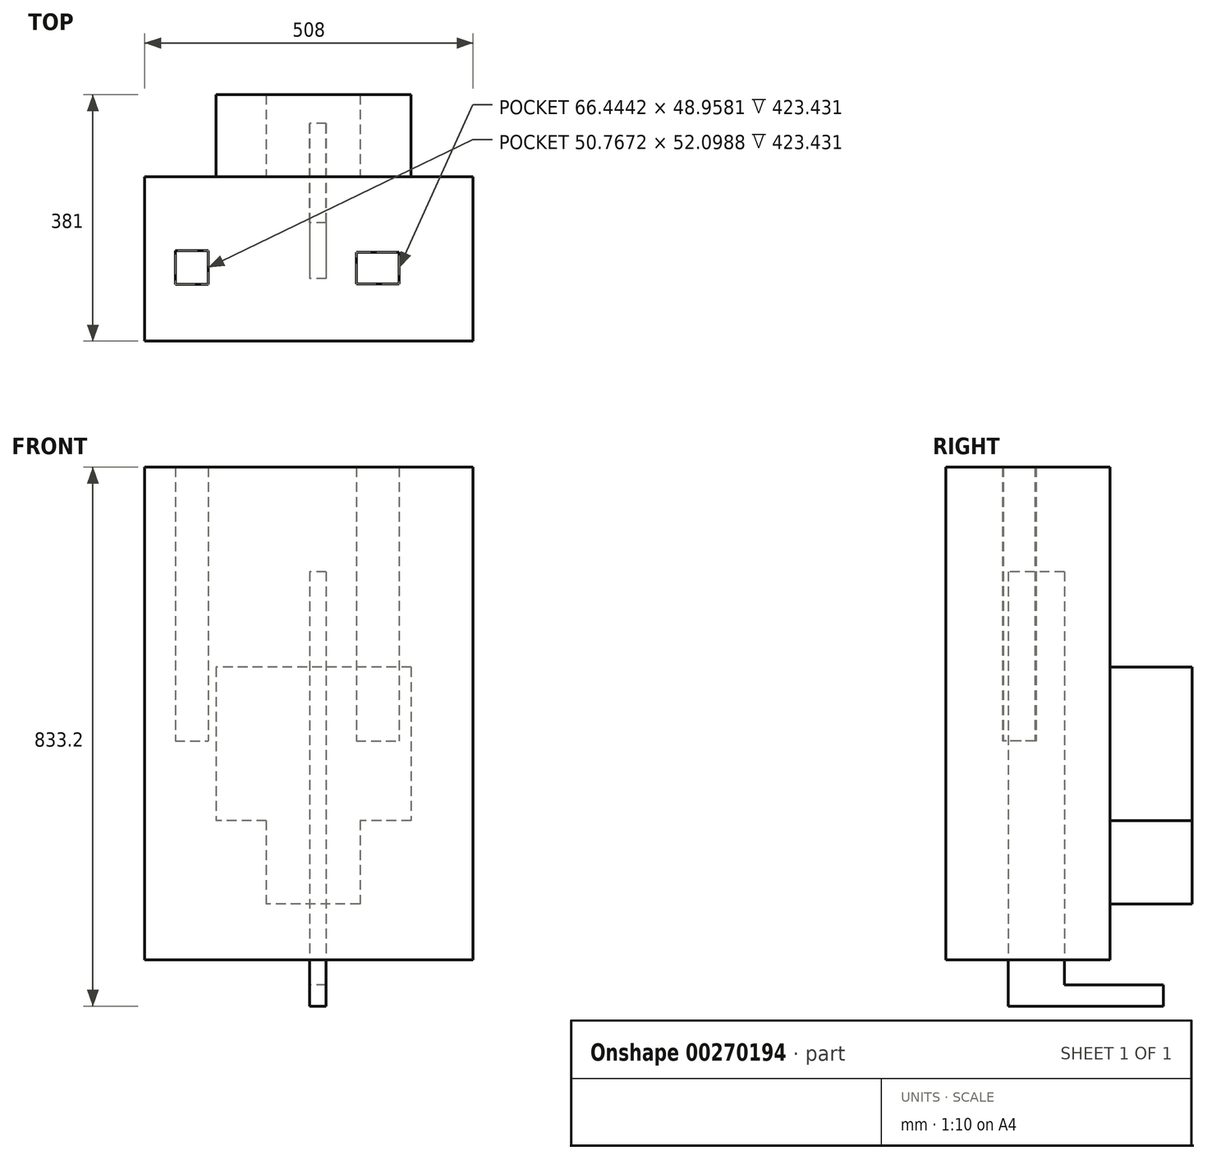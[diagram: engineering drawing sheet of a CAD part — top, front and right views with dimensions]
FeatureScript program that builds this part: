
annotation { "Feature Type Name" : "Feature", "Feature Type Description" : "" }
export const myFeature = defineFeature(function(context is Context, id is Id, definition is map)
    precondition{}
    {
        {
            var Q0;
            Q0=qCreatedBy(makeId("Front.planeOp"),FACE);
            var sketch = newSketch(context, id + "F0", { "sketchPlane" : qUnion([Q0])});
            skLineSegment(sketch, "E0.bottom", {"start": v(-255.3, 423.43) * mm, "end": v(252.7, 423.43) * mm});
            skLineSegment(sketch, "E0.top", {"start": v(-255.3, -338.57) * mm, "end": v(252.7, -338.57) * mm});
            skLineSegment(sketch, "E0.left", {"start": v(-255.3, 423.43) * mm, "end": v(-255.3, -338.57) * mm});
            skLineSegment(sketch, "E0.right", {"start": v(252.7, 423.43) * mm, "end": v(252.7, -338.57) * mm});
            skSolve(sketch);
        }
        {
            var Q0;
            Q0 = qSketchRegion(id + "F0", true);
            extrude(context, id + "F1", {"entities" : qUnion([Q0]), "depth" : 254 * mm});
        }
        {
            var Q0;
            Q0=qCreatedBy(makeId("Front.planeOp"),FACE);
            var sketch = newSketch(context, id + "F2", { "sketchPlane" : qUnion([Q0])});
            skLineSegment(sketch, "E1.bottom", {"start": v(156.8, 114.3) * mm, "end": v(-145.03, 114.3) * mm});
            skLineSegment(sketch, "E1.top", {"start": v(156.8, -122.86) * mm, "end": v(-145.03, -122.86) * mm});
            skLineSegment(sketch, "E1.left", {"start": v(156.8, 114.3) * mm, "end": v(156.8, -122.86) * mm});
            skLineSegment(sketch, "E1.right", {"start": v(-145.03, 114.3) * mm, "end": v(-145.03, -122.86) * mm});
            skLineSegment(sketch, "E2.bottom", {"start": v(77.75, -122.86) * mm, "end": v(-67.18, -122.86) * mm});
            skLineSegment(sketch, "E2.top", {"start": v(77.75, -252.22) * mm, "end": v(-67.18, -252.22) * mm});
            skLineSegment(sketch, "E2.left", {"start": v(77.75, -122.86) * mm, "end": v(77.75, -252.22) * mm});
            skLineSegment(sketch, "E2.right", {"start": v(-67.18, -122.86) * mm, "end": v(-67.18, -252.22) * mm});
            skSolve(sketch);
        }
        {
            var Q0;
            Q0 = qSketchRegion(id + "F2", true);
            extrude(context, id + "F3", {"entities" : qUnion([Q0]), "oppositeDirection" : true, "depth" : 127 * mm});
        }
        {
            var Q0;
            Q0=qCreatedBy(makeId("Right.planeOp"),FACE);
            var sketch = newSketch(context, id + "F4", { "sketchPlane" : qUnion([Q0])});
            skLineSegment(sketch, "E3.bottom", {"start": v(-70.87, 261.89) * mm, "end": v(-157.43, 261.89) * mm});
            skLineSegment(sketch, "E3.top", {"start": v(-70.87, -409.77) * mm, "end": v(-157.43, -409.77) * mm});
            skLineSegment(sketch, "E3.left", {"start": v(-70.87, 261.89) * mm, "end": v(-70.87, -409.77) * mm});
            skLineSegment(sketch, "E3.right", {"start": v(-157.43, 261.89) * mm, "end": v(-157.43, -409.77) * mm});
            skPoint(sketch, "E4.oppositeSnap0", {"position": v(-114.15, -409.77) * mm});
            skLineSegment(sketch, "E4.bottom", {"start": v(-70.87, -377.02) * mm, "end": v(82.55, -377.02) * mm});
            skLineSegment(sketch, "E4.top", {"start": v(-70.87, -409.77) * mm, "end": v(82.55, -409.77) * mm});
            skLineSegment(sketch, "E4.left", {"start": v(-70.87, -377.02) * mm, "end": v(-70.87, -409.77) * mm});
            skLineSegment(sketch, "E4.right", {"start": v(82.55, -377.02) * mm, "end": v(82.55, -409.77) * mm});
            skSolve(sketch);
        }
        {
            var Q0;
            Q0 = qSketchRegion(id + "F4", true);
            extrude(context, id + "F5", {"entities" : qUnion([Q0]), "depth" : 25.4 * mm});
        }
        {
            var Q0;
            Q0=qCreatedBy(makeId("Top.planeOp"),FACE);
            var sketch = newSketch(context, id + "F6", { "sketchPlane" : qUnion([Q0])});
            skLineSegment(sketch, "E5.bottom", {"start": v(-207.9, -114.3) * mm, "end": v(-157.13, -114.3) * mm});
            skLineSegment(sketch, "E5.top", {"start": v(-207.9, -166.4) * mm, "end": v(-157.13, -166.4) * mm});
            skLineSegment(sketch, "E5.left", {"start": v(-207.9, -114.3) * mm, "end": v(-207.9, -166.4) * mm});
            skLineSegment(sketch, "E5.right", {"start": v(-157.13, -114.3) * mm, "end": v(-157.13, -166.4) * mm});
            skLineSegment(sketch, "E6.bottom", {"start": v(72.04, -116.3) * mm, "end": v(138.49, -116.3) * mm});
            skLineSegment(sketch, "E6.top", {"start": v(72.04, -165.25) * mm, "end": v(138.49, -165.25) * mm});
            skLineSegment(sketch, "E6.left", {"start": v(72.04, -116.3) * mm, "end": v(72.04, -165.25) * mm});
            skLineSegment(sketch, "E6.right", {"start": v(138.49, -116.3) * mm, "end": v(138.49, -165.25) * mm});
            skSolve(sketch);
        }
        {
            var Q0;
            Q0 = qSketchRegion(id + "F6", true);
            extrude(context, id + "F7", {"entities" : qUnion([Q0]), "operationType" : NewBodyOperationType.REMOVE, "depth" : 508 * mm});
        }
    });
